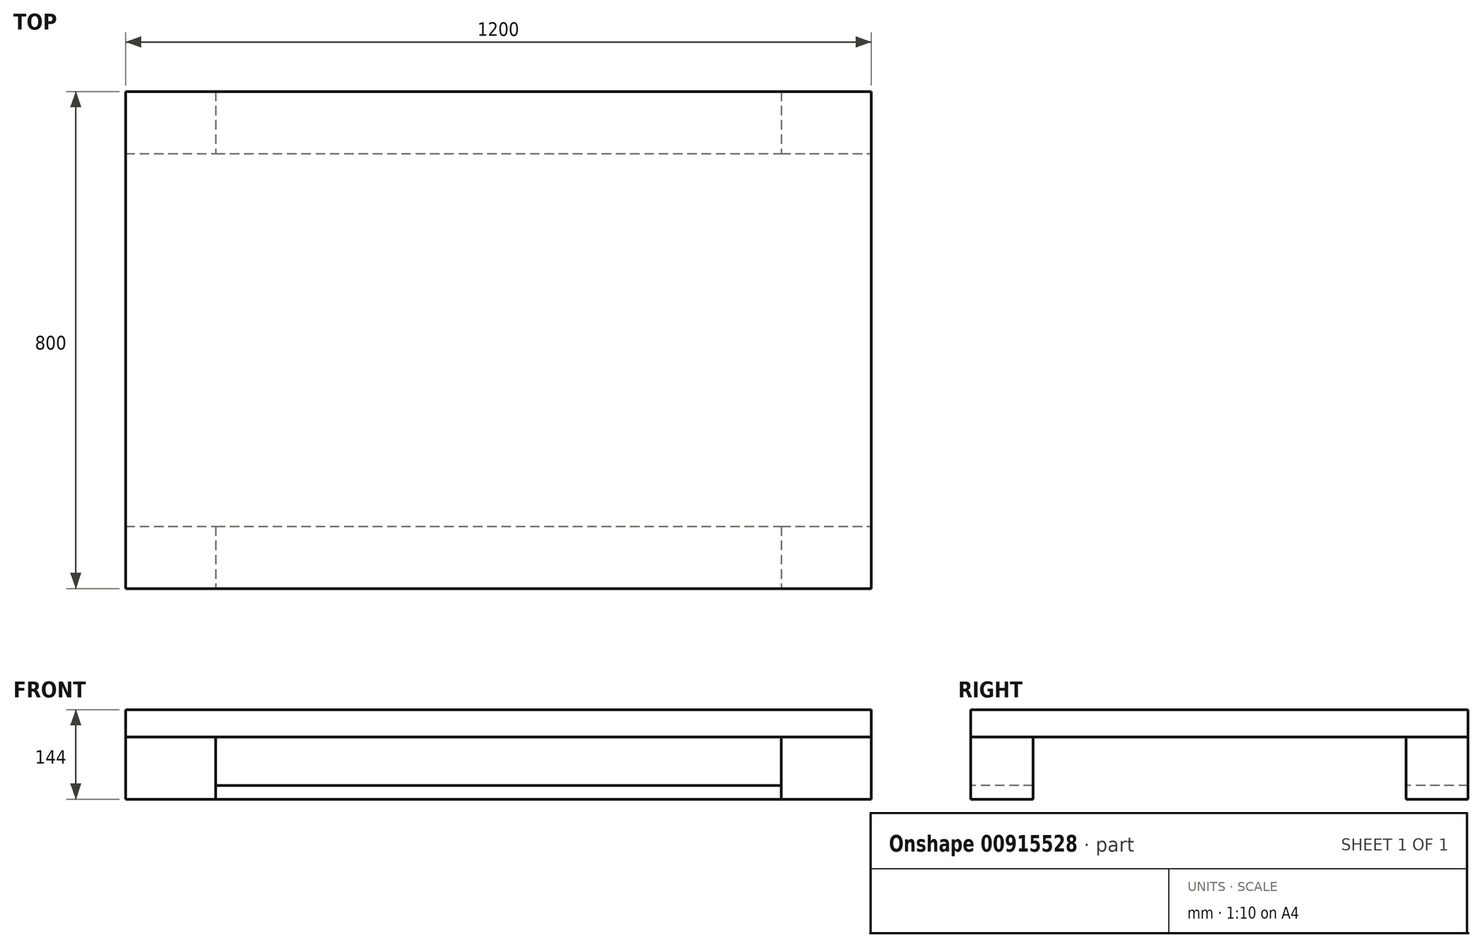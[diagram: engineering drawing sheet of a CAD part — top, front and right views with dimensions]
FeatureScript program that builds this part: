
annotation { "Feature Type Name" : "Feature", "Feature Type Description" : "" }
export const myFeature = defineFeature(function(context is Context, id is Id, definition is map)
    precondition{}
    {
        {
            var Q0;
            Q0=qCreatedBy(makeId("Top.planeOp"),FACE);
            var sketch = newSketch(context, id + "F0", { "sketchPlane" : qUnion([Q0])});
            skLineSegment(sketch, "E0.bottom", {"start": v(600, 400) * mm, "end": v(-600, 400) * mm});
            skLineSegment(sketch, "E0.top", {"start": v(600, -400) * mm, "end": v(-600, -400) * mm});
            skLineSegment(sketch, "E0.left", {"start": v(600, 400) * mm, "end": v(600, -400) * mm});
            skLineSegment(sketch, "E0.right", {"start": v(-600, 400) * mm, "end": v(-600, -400) * mm});
            skPoint(sketch, "E0.middle", {"position": v(0, 0) * mm});
            skLineSegment(sketch, "E1", {"start": v(-455, 400) * mm, "end": v(-455, -413.15) * mm});
            skLineSegment(sketch, "E2", {"start": v(-600, -300) * mm, "end": v(600, -300) * mm});
            skLineSegment(sketch, "E3", {"start": v(455, 400) * mm, "end": v(455, -400) * mm});
            skLineSegment(sketch, "E4", {"start": v(-600, 300) * mm, "end": v(600, 300) * mm});
            skSolve(sketch);
        }
        {
            var Q0;
            {var subQ0=sQuery(id+"F0.wireOp",EDGE,"E1");var subQ1=sQuery(id+"F0.wireOp",EDGE,"E0.bottom");var subQ2=makeQuery(id+"F0.imprint","INTERSECT",VERTEX,{"derivedFrom":[subQ1,subQ0]});Q0=makeQuery(id+"F0.imprint","IMPRINT",FACE,{"disambiguationData":[TD([[makeQuery(id+"F0.imprint","IMPRINT",EDGE,{"disambiguationData":[TD([[subQ2,1.0]])],"derivedFrom":subQ1}),1.0]])]});}
            var Q1;
            {var subQ0=sQuery(id+"F0.wireOp",EDGE,"E3");var subQ1=sQuery(id+"F0.wireOp",EDGE,"E0.top");var subQ2=makeQuery(id+"F0.imprint","INTERSECT",VERTEX,{"derivedFrom":[subQ1,subQ0]});Q1=makeQuery(id+"F0.imprint","IMPRINT",FACE,{"disambiguationData":[TD([[makeQuery(id+"F0.imprint","IMPRINT",EDGE,{"disambiguationData":[TD([[subQ2,-1.0]])],"derivedFrom":subQ1}),-1.0]])]});}
            extrude(context, id + "F1", {"entities" : qUnion([Q0, Q1]), "depth" : 22 * mm});
        }
        {
            var Q0;
            {var subQ0=sQuery(id+"F0.wireOp",EDGE,"E0.left");var subQ1=sQuery(id+"F0.wireOp",EDGE,"E0.top");var subQ2=makeQuery(id+"F0.imprint","INTERSECT",VERTEX,{"derivedFrom":[subQ1,subQ0]});Q0=makeQuery(id+"F0.imprint","IMPRINT",FACE,{"disambiguationData":[TD([[makeQuery(id+"F0.imprint","IMPRINT",EDGE,{"disambiguationData":[TD([[subQ2,-1.0]])],"derivedFrom":subQ1}),-1.0]])]});}
            var Q1;
            {var subQ0=sQuery(id+"F0.wireOp",EDGE,"E0.right");var subQ1=sQuery(id+"F0.wireOp",EDGE,"E0.top");var subQ2=makeQuery(id+"F0.imprint","INTERSECT",VERTEX,{"derivedFrom":[subQ1,subQ0]});Q1=makeQuery(id+"F0.imprint","IMPRINT",FACE,{"disambiguationData":[TD([[makeQuery(id+"F0.imprint","IMPRINT",EDGE,{"disambiguationData":[TD([[subQ2,1.0]])],"derivedFrom":subQ1}),-1.0]])]});}
            var Q2;
            {var subQ0=sQuery(id+"F0.wireOp",EDGE,"E0.right");var subQ1=sQuery(id+"F0.wireOp",EDGE,"E0.bottom");var subQ2=makeQuery(id+"F0.imprint","INTERSECT",VERTEX,{"derivedFrom":[subQ1,subQ0]});Q2=makeQuery(id+"F0.imprint","IMPRINT",FACE,{"disambiguationData":[TD([[makeQuery(id+"F0.imprint","IMPRINT",EDGE,{"disambiguationData":[TD([[subQ2,1.0]])],"derivedFrom":subQ1}),1.0]])]});}
            var Q3;
            {var subQ0=sQuery(id+"F0.wireOp",EDGE,"E0.left");var subQ1=sQuery(id+"F0.wireOp",EDGE,"E0.bottom");var subQ2=makeQuery(id+"F0.imprint","INTERSECT",VERTEX,{"derivedFrom":[subQ1,subQ0]});Q3=makeQuery(id+"F0.imprint","IMPRINT",FACE,{"disambiguationData":[TD([[makeQuery(id+"F0.imprint","IMPRINT",EDGE,{"disambiguationData":[TD([[subQ2,-1.0]])],"derivedFrom":subQ1}),1.0]])]});}
            extrude(context, id + "F2", {"entities" : qUnion([Q0, Q1, Q2, Q3]), "depth" : 100 * mm});
        }
        {
            var Q0;
            Q0=makeQuery(id+"F2.opExtrude","CAP_FACE",FACE,{"disambiguationData":[OSD([sQuery(id+"F0.wireOp",EDGE,"E0.top"),sQuery(id+"F0.wireOp",EDGE,"E0.left"),sQuery(id+"F0.wireOp",EDGE,"E2"),sQuery(id+"F0.wireOp",EDGE,"E3")])],"isStart":false});
            var sketch = newSketch(context, id + "F3", { "sketchPlane" : qUnion([Q0])});
            skLineSegment(sketch, "E5.bottom", {"start": v(600, -400) * mm, "end": v(-600, -400) * mm});
            skLineSegment(sketch, "E5.top", {"start": v(600, 400) * mm, "end": v(-600, 400) * mm});
            skLineSegment(sketch, "E5.left", {"start": v(600, -400) * mm, "end": v(600, 400) * mm});
            skLineSegment(sketch, "E5.right", {"start": v(-600, -400) * mm, "end": v(-600, 400) * mm});
            skSolve(sketch);
        }
        {
            var Q0;
            Q0=qSketchRegion(id+"F3",true);
            extrude(context, id + "F4", {"entities" : qUnion([Q0]), "depth" : 44 * mm});
        }
    });
